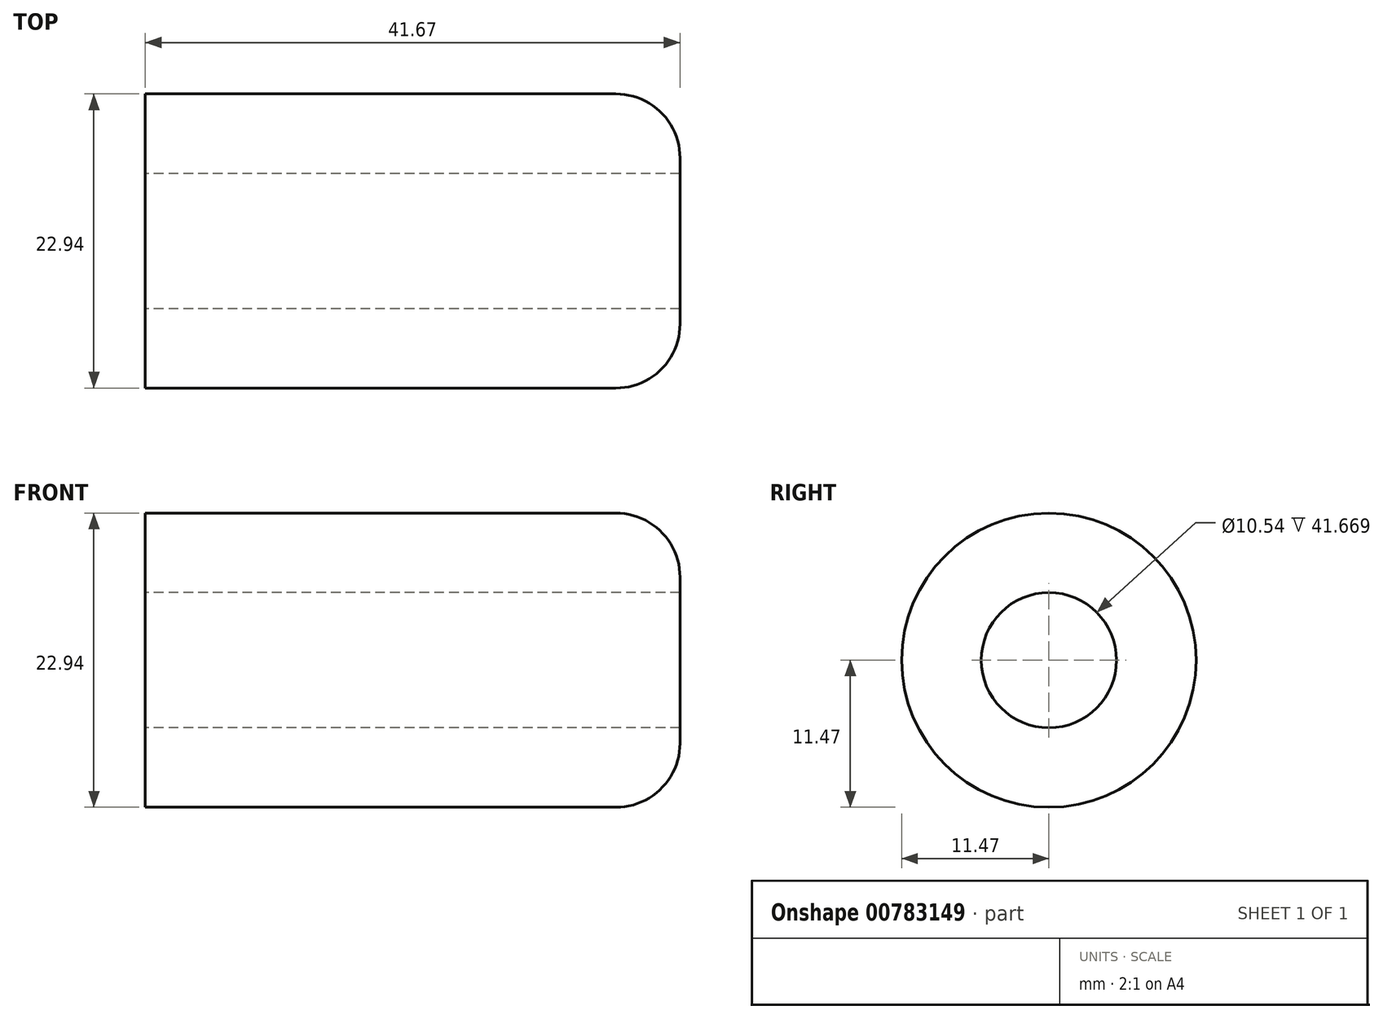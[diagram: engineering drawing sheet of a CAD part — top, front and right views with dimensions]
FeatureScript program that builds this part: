
annotation { "Feature Type Name" : "Feature", "Feature Type Description" : "" }
export const myFeature = defineFeature(function(context is Context, id is Id, definition is map)
    precondition{}
    {
        {
            var Q0;
            Q0=qCreatedBy(makeId("Front.planeOp"),FACE);
            var sketch = newSketch(context, id + "F0", { "sketchPlane" : qUnion([Q0])});
            skLineSegment(sketch, "E0.bottom", {"start": v(-18.42, 11.47) * mm, "end": v(18.25, 11.47) * mm});
            skLineSegment(sketch, "E0.top", {"start": v(-18.42, 5.27) * mm, "end": v(23.25, 5.27) * mm});
            skLineSegment(sketch, "E0.left", {"start": v(-18.42, 11.47) * mm, "end": v(-18.42, 5.27) * mm});
            skLineSegment(sketch, "E0.right", {"start": v(23.25, 6.47) * mm, "end": v(23.25, 5.27) * mm});
            skPoint(sketch, "E1.visualSharp", {"position": v(23.25, 11.47) * mm});
            skArc(sketch, "E1.filletArc", {"start": v(23.25, 6.47) * mm, "mid": v(21.79, 10) * mm, "end": v(18.25, 11.47) * mm});
            skLineSegment(sketch, "E2", {"start": v(-22.38, 0) * mm, "end": v(27.97, 0) * mm});
            skSolve(sketch);
        }
        {
            var Q0;
            Q0 = qSketchRegion(id + "F0", true);
            var Q1;
            Q1=sQuery(id+"F0.wireOp",EDGE,"E2");
            revolve(context, id + "F1", {"surfaceOperationType" : NewSurfaceOperationType.NEW, "entities" : qUnion([Q0]), "axis" : qUnion([Q1]), "revolveType" : RevolveType.FULL});
        }
    });
